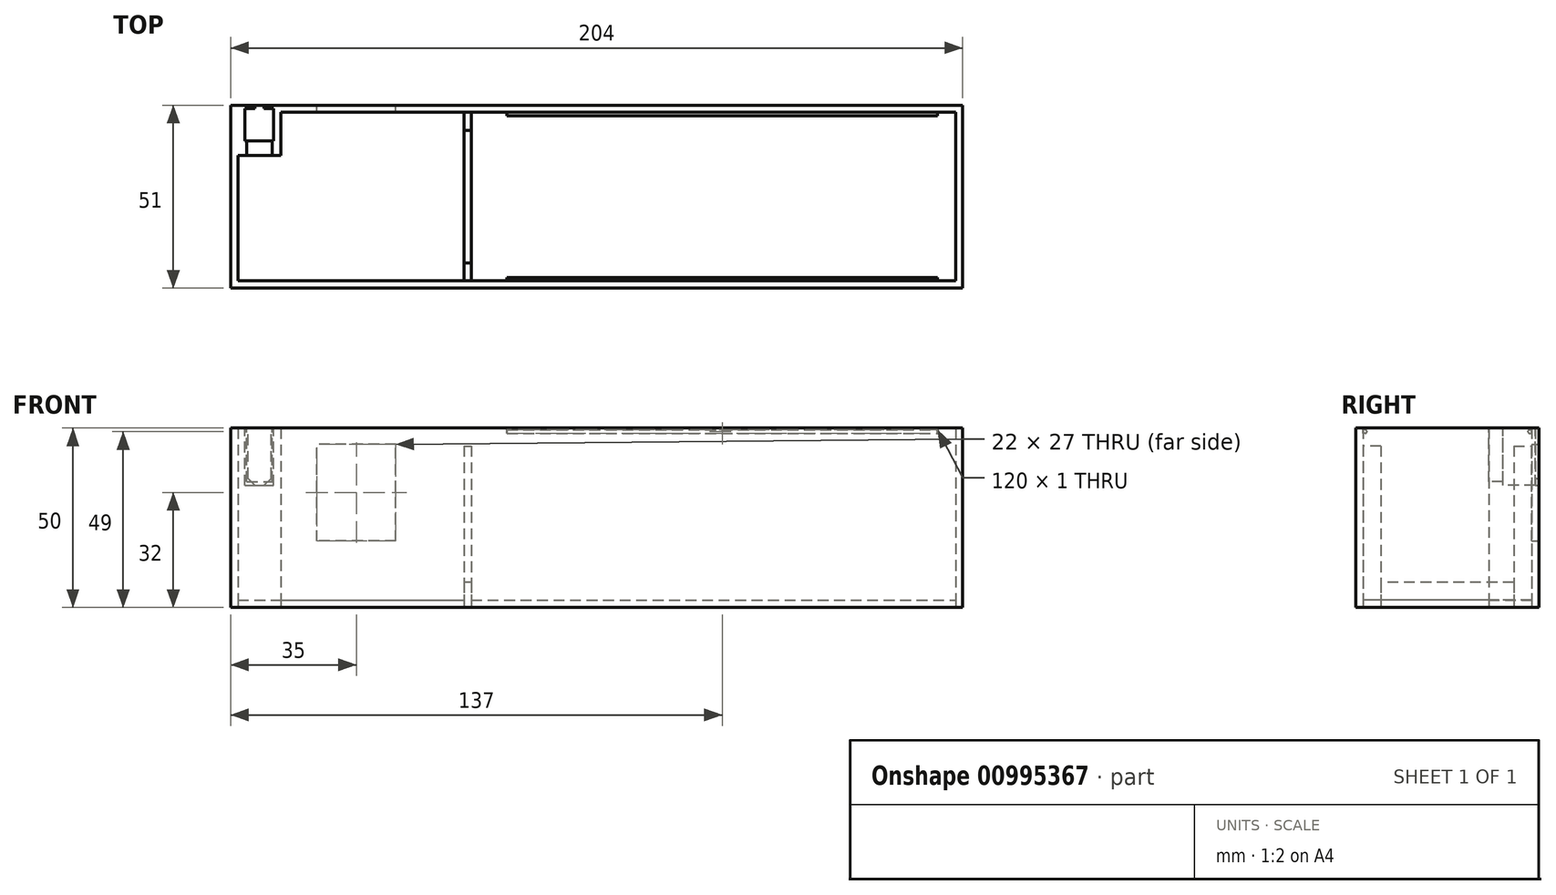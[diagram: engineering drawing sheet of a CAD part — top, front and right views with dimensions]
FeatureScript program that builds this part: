
annotation { "Feature Type Name" : "Feature", "Feature Type Description" : "" }
export const myFeature = defineFeature(function(context is Context, id is Id, definition is map)
    precondition{}
    {
        {
            var Q0;
            Q0=qCreatedBy(makeId("Top.planeOp"),FACE);
            var sketch = newSketch(context, id + "F0", { "sketchPlane" : qUnion([Q0])});
            skLineSegment(sketch, "E0.bottom", {"start": v(0, 0) * mm, "end": v(200, 0) * mm});
            skLineSegment(sketch, "E0.top", {"start": v(0, -47) * mm, "end": v(200, -47) * mm});
            skLineSegment(sketch, "E0.left", {"start": v(0, 0) * mm, "end": v(0, -47) * mm});
            skLineSegment(sketch, "E0.right", {"start": v(200, 0) * mm, "end": v(200, -47) * mm});
            skLineSegment(sketch, "E1.0", {"start": v(-2, 2) * mm, "end": v(202, 2) * mm});
            skLineSegment(sketch, "E1.1", {"start": v(-2, 2) * mm, "end": v(-2, -49) * mm});
            skLineSegment(sketch, "E1.2", {"start": v(-2, -49) * mm, "end": v(202, -49) * mm});
            skLineSegment(sketch, "E1.3", {"start": v(202, 2) * mm, "end": v(202, -49) * mm});
            skLineSegment(sketch, "E2", {"start": v(65, 0) * mm, "end": v(65, -5) * mm});
            skLineSegment(sketch, "E3", {"start": v(65, -5) * mm, "end": v(63, -5) * mm});
            skLineSegment(sketch, "E4", {"start": v(63, -5) * mm, "end": v(63, 0) * mm});
            skLineSegment(sketch, "E5", {"start": v(65, -47) * mm, "end": v(65, -42) * mm});
            skLineSegment(sketch, "E6", {"start": v(65, -42) * mm, "end": v(63, -42) * mm});
            skLineSegment(sketch, "E7", {"start": v(63, -42) * mm, "end": v(63, -47) * mm});
            skLineSegment(sketch, "E8", {"start": v(0, -12) * mm, "end": v(12, -12) * mm});
            skLineSegment(sketch, "E9", {"start": v(12, -12) * mm, "end": v(12, 0) * mm});
            skLineSegment(sketch, "E10", {"start": v(63, -42) * mm, "end": v(63, -5) * mm});
            skLineSegment(sketch, "E11", {"start": v(65, -5) * mm, "end": v(65, -42) * mm});
            skSolve(sketch);
        }
        {
            var Q0;
            {var subQ1=sQuery(id+"F0.wireOp",EDGE,"E0.right");Q0=makeQuery(id+"F0.imprint","IMPRINT",FACE,{"disambiguationData":[TD([[makeQuery(id+"F0.imprint","IMPRINT",EDGE,{"derivedFrom":subQ1}),-1.0]])]});}
            var Q1;
            {var subQ5=sQuery(id+"F0.wireOp",EDGE,"E4");Q1=makeQuery(id+"F0.imprint","IMPRINT",FACE,{"disambiguationData":[TD([[makeQuery(id+"F0.imprint","IMPRINT",EDGE,{"derivedFrom":subQ5}),1.0]])]});}
            extrude(context, id + "F1", {"entities" : qUnion([Q0, Q1]), "depth" : 2 * mm, "offsetDistance" : 25 * mm});
        }
        {
            var Q0;
            {var subQ4=sQuery(id+"F0.wireOp",EDGE,"E8");Q0=makeQuery(id+"F0.imprint","IMPRINT",FACE,{"disambiguationData":[TD([[makeQuery(id+"F0.imprint","IMPRINT",EDGE,{"derivedFrom":subQ4}),1.0]])]});}
            var Q1;
            {var subQ0=sQuery(id+"F0.wireOp",EDGE,"E0.right");Q1=makeQuery(id+"F0.imprint","IMPRINT",FACE,{"disambiguationData":[TD([[makeQuery(id+"F0.imprint","IMPRINT",EDGE,{"derivedFrom":subQ0}),1.0]])]});}
            extrude(context, id + "F2", {"entities" : qUnion([Q0, Q1]), "depth" : 50 * mm, "offsetDistance" : 25 * mm});
        }
        {
            var Q0;
            Q0=makeQuery(id+"F12.imprint","IMPRINT",FACE,{"disambiguationData":[TD([[makeQuery(id+"F12.imprint","IMPRINT",EDGE,{"derivedFrom":sQuery(id+"F12.wireOp",EDGE,"E31.bottom")}),-1.0]])]});
            var Q1;
            Q1=makeQuery(id+"F0.imprint","IMPRINT",FACE,{"disambiguationData":[TD([[makeQuery(id+"F0.imprint","IMPRINT",EDGE,{"derivedFrom":sQuery(id+"F0.wireOp",EDGE,"E3")}),1.0]])]});
            extrude(context, id + "F3", {"entities" : qUnion([Q0, Q1]), "operationType" : NewBodyOperationType.ADD, "depth" : 7 * mm, "offsetDistance" : 25 * mm});
        }
        {
            var Q0;
            {var subQ0=sQuery(id+"F0.wireOp",EDGE,"E5");Q0=makeQuery(id+"F0.imprint","IMPRINT",FACE,{"disambiguationData":[TD([[makeQuery(id+"F0.imprint","IMPRINT",EDGE,{"derivedFrom":subQ0}),1.0]])]});}
            var Q1;
            {var subQ0=sQuery(id+"F0.wireOp",EDGE,"E2");Q1=makeQuery(id+"F0.imprint","IMPRINT",FACE,{"disambiguationData":[TD([[makeQuery(id+"F0.imprint","IMPRINT",EDGE,{"derivedFrom":subQ0}),-1.0]])]});}
            extrude(context, id + "F4", {"entities" : qUnion([Q0, Q1]), "depth" : 45 * mm, "offsetDistance" : 25 * mm});
        }
        {
            var Q0;
            Q0=makeQuery(id+"F2.opExtrude","CAP_FACE",FACE,{"disambiguationData":[OSD([sQuery(id+"F0.wireOp",EDGE,"E0.bottom"),sQuery(id+"F0.wireOp",EDGE,"E0.top"),sQuery(id+"F0.wireOp",EDGE,"E0.left"),sQuery(id+"F0.wireOp",EDGE,"E0.right"),sQuery(id+"F0.wireOp",EDGE,"E1.0"),sQuery(id+"F0.wireOp",EDGE,"E1.1"),sQuery(id+"F0.wireOp",EDGE,"E1.2"),sQuery(id+"F0.wireOp",EDGE,"E1.3"),sQuery(id+"F0.wireOp",EDGE,"E2"),sQuery(id+"F0.wireOp",EDGE,"E3"),sQuery(id+"F0.wireOp",EDGE,"E4"),sQuery(id+"F0.wireOp",EDGE,"E5"),sQuery(id+"F0.wireOp",EDGE,"E6"),sQuery(id+"F0.wireOp",EDGE,"E7"),sQuery(id+"F0.wireOp",EDGE,"E8"),sQuery(id+"F0.wireOp",EDGE,"E9")])],"isStart":false});
            var sketch = newSketch(context, id + "F5", { "sketchPlane" : qUnion([Q0])});
            skLineSegment(sketch, "E12", {"start": v(6, 8.8) * mm, "end": v(6, -16.73) * mm, "construction": true});
            skLineSegment(sketch, "E13.bottom", {"start": v(2.75, 1) * mm, "end": v(9.25, 1) * mm});
            skLineSegment(sketch, "E13.top", {"start": v(2.75, 3) * mm, "end": v(9.25, 3) * mm});
            skLineSegment(sketch, "E13.left", {"start": v(2.75, 1) * mm, "end": v(2.75, 3) * mm});
            skLineSegment(sketch, "E13.right", {"start": v(9.25, 1) * mm, "end": v(9.25, 3) * mm});
            skPoint(sketch, "E13.middle", {"position": v(6, 2) * mm});
            skLineSegment(sketch, "E14", {"start": v(2.75, 1) * mm, "end": v(2, 1) * mm});
            skLineSegment(sketch, "E15", {"start": v(2, 1) * mm, "end": v(2, -8) * mm});
            skLineSegment(sketch, "E16", {"start": v(2, -8) * mm, "end": v(10, -8) * mm});
            skLineSegment(sketch, "E17", {"start": v(10, -8) * mm, "end": v(10, 1) * mm});
            skLineSegment(sketch, "E18", {"start": v(10, 1) * mm, "end": v(9.25, 1) * mm});
            skLineSegment(sketch, "E19", {"start": v(2, -8) * mm, "end": v(2, -12) * mm});
            skLineSegment(sketch, "E20", {"start": v(10, -8) * mm, "end": v(10, -12) * mm});
            skLineSegment(sketch, "E21", {"start": v(2.5, -8) * mm, "end": v(2.5, -12) * mm});
            skLineSegment(sketch, "E22", {"start": v(9.5, -8) * mm, "end": v(9.5, -12) * mm});
            skSolve(sketch);
        }
        {
            var Q0;
            Q0=makeQuery(id+"F5.imprint","IMPRINT",FACE,{"disambiguationData":[TD([[makeQuery(id+"F5.imprint","IMPRINT",EDGE,{"derivedFrom":sQuery(id+"F5.wireOp",EDGE,"E13.bottom")}),-1.0]])]});
            extrude(context, id + "F6", {"entities" : qUnion([Q0]), "operationType" : NewBodyOperationType.REMOVE, "oppositeDirection" : true, "depth" : 16 * mm, "offsetDistance" : 25 * mm});
        }
        {
            var Q0;
            {var subQ0=sQuery(id+"F5.wireOp",EDGE,"E21");Q0=makeQuery(id+"F5.imprint","IMPRINT",FACE,{"disambiguationData":[TD([[makeQuery(id+"F5.imprint","IMPRINT",EDGE,{"derivedFrom":subQ0}),1.0]])]});}
            extrude(context, id + "F7", {"entities" : qUnion([Q0]), "operationType" : NewBodyOperationType.REMOVE, "oppositeDirection" : true, "depth" : 15 * mm, "offsetDistance" : 25 * mm});
        }
        {
            var Q0;
            Q0=makeQuery(id+"F2.opExtrude","SWEPT_FACE",FACE,{"disambiguationData":[OSD([sQuery(id+"F0.wireOp",EDGE,"E1.0")])]});
            var sketch = newSketch(context, id + "F8", { "sketchPlane" : qUnion([Q0])});
            skLineSegment(sketch, "E23.bottom", {"start": v(-2.77, 34) * mm, "end": v(-9.27, 34) * mm});
            skLineSegment(sketch, "E23.top", {"start": v(-2.77, 66) * mm, "end": v(-9.27, 66) * mm});
            skLineSegment(sketch, "E23.left", {"start": v(-2.77, 34) * mm, "end": v(-2.77, 66) * mm});
            skLineSegment(sketch, "E23.right", {"start": v(-9.27, 34) * mm, "end": v(-9.27, 66) * mm});
            skPoint(sketch, "E23.middle", {"position": v(-6.02, 50) * mm});
            skLineSegment(sketch, "E24", {"start": v(-7.27, 34) * mm, "end": v(-9.27, 36) * mm});
            skLineSegment(sketch, "E25", {"start": v(-4.77, 34) * mm, "end": v(-2.77, 36) * mm});
            skPoint(sketch, "E26", {"position": v(-33, 32) * mm});
            skLineSegment(sketch, "E27.bottom", {"start": v(-44, 18.5) * mm, "end": v(-22, 18.5) * mm});
            skLineSegment(sketch, "E27.top", {"start": v(-44, 45.5) * mm, "end": v(-22, 45.5) * mm});
            skLineSegment(sketch, "E27.left", {"start": v(-44, 18.5) * mm, "end": v(-44, 45.5) * mm});
            skLineSegment(sketch, "E27.right", {"start": v(-22, 18.5) * mm, "end": v(-22, 45.5) * mm});
            skSolve(sketch);
        }
        {
            var Q0;
            {var subQ0=sQuery(id+"F8.wireOp",EDGE,"E24");Q0=makeQuery(id+"F8.imprint","IMPRINT",FACE,{"disambiguationData":[TD([[makeQuery(id+"F8.imprint","IMPRINT",EDGE,{"derivedFrom":subQ0}),-1.0]])]});}
            var Q1;
            Q1=makeQuery(id+"F8.imprint","IMPRINT",FACE,{"disambiguationData":[TD([[makeQuery(id+"F8.imprint","IMPRINT",EDGE,{"derivedFrom":sQuery(id+"F8.wireOp",EDGE,"E27.bottom")}),1.0]])]});
            extrude(context, id + "F9", {"entities" : qUnion([Q0, Q1]), "operationType" : NewBodyOperationType.REMOVE, "oppositeDirection" : true, "depth" : 5 * mm, "offsetDistance" : 25 * mm});
        }
        {
            var Q0;
            Q0=makeQuery(id+"F2.opExtrude","SWEPT_FACE",FACE,{"disambiguationData":[OSD([sQuery(id+"F0.wireOp",EDGE,"E1.2")])]});
            var sketch = newSketch(context, id + "F10", { "sketchPlane" : qUnion([Q0])});
            skPoint(sketch, "E28", {"position": v(135, 49) * mm});
            skLineSegment(sketch, "E29.bottom", {"start": v(75, 49.5) * mm, "end": v(195, 49.5) * mm});
            skLineSegment(sketch, "E29.top", {"start": v(75, 48.5) * mm, "end": v(195, 48.5) * mm});
            skLineSegment(sketch, "E29.left", {"start": v(75, 49.5) * mm, "end": v(75, 48.5) * mm});
            skLineSegment(sketch, "E29.right", {"start": v(195, 49.5) * mm, "end": v(195, 48.5) * mm});
            skSolve(sketch);
        }
        {
            var Q0;
            Q0=makeQuery(id+"F10.imprint","IMPRINT",FACE,{"disambiguationData":[TD([[makeQuery(id+"F10.imprint","IMPRINT",EDGE,{"derivedFrom":sQuery(id+"F10.wireOp",EDGE,"E29.bottom")}),-1.0]])]});
            extrude(context, id + "F11", {"entities" : qUnion([Q0]), "operationType" : NewBodyOperationType.ADD, "oppositeDirection" : true, "depth" : 3 * mm, "offsetDistance" : 25 * mm});
        }
        {
            var Q0;
            Q0=makeQuery(id+"F2.opExtrude","SWEPT_FACE",FACE,{"disambiguationData":[OSD([sQuery(id+"F0.wireOp",EDGE,"E1.0")])]});
            var sketch = newSketch(context, id + "F12", { "sketchPlane" : qUnion([Q0])});
            skPoint(sketch, "E30", {"position": v(-135, 49) * mm});
            skLineSegment(sketch, "E31.bottom", {"start": v(-75, 48.5) * mm, "end": v(-195, 48.5) * mm});
            skLineSegment(sketch, "E31.top", {"start": v(-75, 49.5) * mm, "end": v(-195, 49.5) * mm});
            skLineSegment(sketch, "E31.left", {"start": v(-75, 48.5) * mm, "end": v(-75, 49.5) * mm});
            skLineSegment(sketch, "E31.right", {"start": v(-195, 48.5) * mm, "end": v(-195, 49.5) * mm});
            skSolve(sketch);
        }
        {
            var Q0;
            Q0 = qSketchRegion(id + "F12", true);
            extrude(context, id + "F13", {"entities" : qUnion([Q0]), "operationType" : NewBodyOperationType.ADD, "oppositeDirection" : true, "depth" : 3 * mm, "offsetDistance" : 25 * mm});
        }
        {
            var Q0;
            Q0=makeQuery(id+"F11.opExtrude","CAP_EDGE",EDGE,{"disambiguationData":[OSD([sQuery(id+"F10.wireOp",EDGE,"E29.top")])],"isStart":false});
            var Q1;
            Q1=makeQuery(id+"F11.opExtrude","CAP_EDGE",EDGE,{"disambiguationData":[OSD([sQuery(id+"F10.wireOp",EDGE,"E29.bottom")])],"isStart":false});
            var Q2;
            Q2=makeQuery(id+"F13.opExtrude","CAP_EDGE",EDGE,{"disambiguationData":[OSD([sQuery(id+"F12.wireOp",EDGE,"E31.top")])],"isStart":false});
            var Q3;
            Q3=makeQuery(id+"F13.opExtrude","CAP_EDGE",EDGE,{"disambiguationData":[OSD([sQuery(id+"F12.wireOp",EDGE,"E31.bottom")])],"isStart":false});
            fillet(context, id + "F14", {"entities" : qUnion([Q0, Q1, Q2, Q3]), "radius" : 0.4 * mm, "tangentPropagation" : true, "allowEdgeOverflow" : false});
        }
    });
